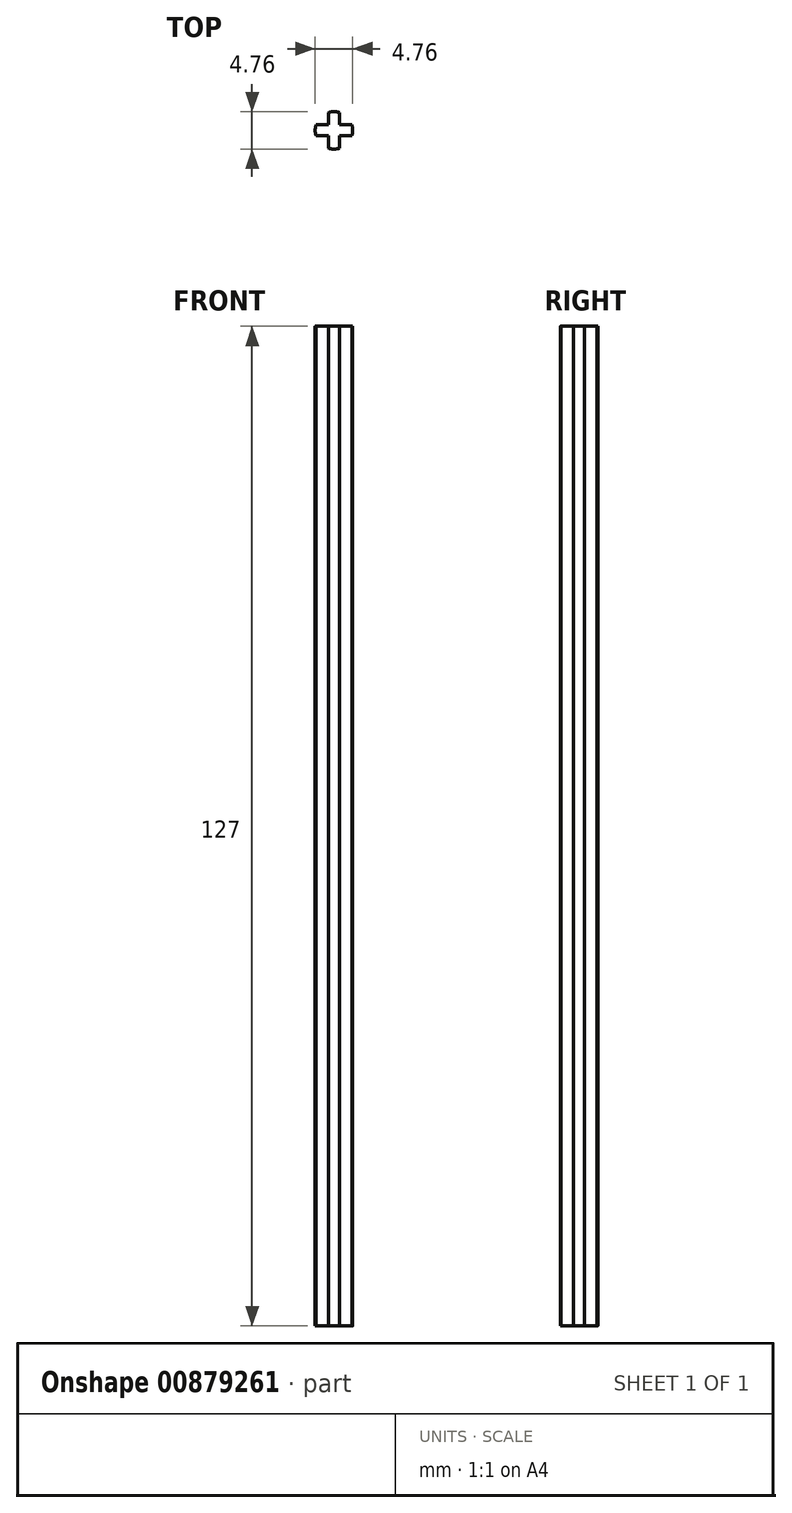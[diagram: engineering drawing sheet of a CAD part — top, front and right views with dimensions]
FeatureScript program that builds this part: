
annotation { "Feature Type Name" : "Feature", "Feature Type Description" : "" }
export const myFeature = defineFeature(function(context is Context, id is Id, definition is map)
    precondition{}
    {
        {
            var Q0;
            Q0=qCreatedBy(makeId("Top.planeOp"),FACE);
            var sketch = newSketch(context, id + "F0", { "sketchPlane" : qUnion([Q0])});
            skArc(sketch, "E0", {"start": v(-11.58, 9.38) * mm, "mid": v(-10.88, 9.28) * mm, "end": v(-10.18, 9.38) * mm});
            skLineSegment(sketch, "E1.bottom", {"start": v(-11.58, 10.96) * mm, "end": v(-13.16, 10.96) * mm});
            skLineSegment(sketch, "E1.left", {"start": v(-11.58, 10.96) * mm, "end": v(-11.58, 9.38) * mm});
            skLineSegment(sketch, "E2.bottom", {"start": v(-10.18, 10.96) * mm, "end": v(-8.6, 10.96) * mm});
            skLineSegment(sketch, "E2.left", {"start": v(-10.18, 10.96) * mm, "end": v(-10.18, 9.38) * mm});
            skLineSegment(sketch, "E3.bottom", {"start": v(-10.18, 12.36) * mm, "end": v(-8.6, 12.36) * mm});
            skLineSegment(sketch, "E3.left", {"start": v(-10.18, 12.36) * mm, "end": v(-10.18, 13.94) * mm});
            skLineSegment(sketch, "E4.bottom", {"start": v(-11.58, 12.36) * mm, "end": v(-13.16, 12.36) * mm});
            skLineSegment(sketch, "E4.left", {"start": v(-11.58, 12.36) * mm, "end": v(-11.58, 13.94) * mm});
            skPoint(sketch, "E5.orphan", {"position": v(-10.88, 9.28) * mm});
            skPoint(sketch, "E4.top.end.orphan", {"position": v(-13.84, 14.05) * mm});
            skArc(sketch, "E6.trimOffspring", {"start": v(-13.16, 12.36) * mm, "mid": v(-13.26, 11.66) * mm, "end": v(-13.16, 10.96) * mm});
            skArc(sketch, "E7.trimOffspring", {"start": v(-10.18, 13.94) * mm, "mid": v(-10.88, 14.04) * mm, "end": v(-11.58, 13.94) * mm});
            skPoint(sketch, "E3.right.end.orphan", {"position": v(-8.3, 14.05) * mm});
            skArc(sketch, "E8.trimOffspring", {"start": v(-8.6, 10.96) * mm, "mid": v(-8.5, 11.66) * mm, "end": v(-8.6, 12.36) * mm});
            skSolve(sketch);
        }
        {
            var Q0;
            Q0=makeQuery(id+"F0.imprint","IMPRINT",FACE,{"disambiguationData":[TD([[makeQuery(id+"F0.imprint","IMPRINT",EDGE,{"derivedFrom":sQuery(id+"F0.wireOp",EDGE,"E0")}),1.0]])]});
            extrude(context, id + "F1", {"entities" : qUnion([Q0]), "depth" : 127 * mm, "offsetDistance" : 25.4 * mm});
        }
    });
